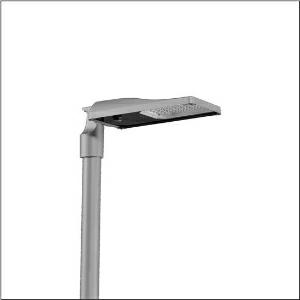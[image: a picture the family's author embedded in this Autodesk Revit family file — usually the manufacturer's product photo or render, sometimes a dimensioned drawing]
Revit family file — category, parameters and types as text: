
# Revit family: streetlight_sl_31_mini___st1_0a_5xh6d3ar08ha_e09e
name_source: partatom
category: Lighting Fixtures
units: mm (PartAtom-declared; Revit-internal decimal feet)

## family parameters
Cut with Voids When Loaded = No
Host = Face
Light Source = No
Part Type = Normal
Room Calculation Point = No
Round Connector Dimension = Use Diameter
Shared = No

## types (1)
- --- (1 x LED, 9230 lm, 68.3 W, 3000K)
    Apparent Load = 68 VA
    CIE Flux Codes = 37 72 97 100 100
    Color Rendering = 70
    Color Temperature = 3000K
    Default Elevation = 1800 mm
    Description = Streetlight SL 31 mini D4i mast luminaire for post-top, side-entry; light control with lens of PMMA; light distribution: ST1.0a, direct asymmetric distribution, for standard-compliant lighting for roads and squares; LED: luminous flux: 9.230lm, light colour: 730, colour temperature: 3000K; luminous efficacy: 135,1lm/W; control: pre-setting: logarithmic dimming characteristic, flexible luminous flux parameterisation, time-dependent luminous flux control, constant luminous flux control, power reduction, intelligent temperature release in ECG and LED module, overheat protection; luminaire housing, of diecast aluminium, Siteco® metallic grey (DB 702S), corrosivity category C5 high according to DIN EN ISO 12944; cover of toughened safety glass, transparent, opened without tools; mast flange of diecast aluminium, Siteco® metallic grey (DB 702S), spigot size: 76/60mm, mast flange included unmounted; with cable H07RN-F 2x 1.5mm², cable length: 8,5m, connection cable pre-assembled; mains connection: 220..240V, AC, 50/60Hz; power consumption (at start of service life): 68,3W / (at end of service life): 74,5W / (with reduced operation 50%): 29,5W; protection rating (complete): IP66; insulation class (complete): insulation class II (safety insulation); impact resistance: IK09; certification: CE, ENEC, ENEC+, VDE, UKCA, ZD4i; permissible operating ambient temperature for outdoor applications: -40..+50°C; packaging unit: 1 piece

Light Distribution: ST1.0a
    Height = 76 mm
    Lamp = 1 x LED
    Lamp Light Flux = 9230 lm
    Lamp Power = 68.3 W
    Lamp count = 1
    Length = 547 mm
    Luminous efficacy = 135 lm/W
    Manufacturer = Siteco
    ModVariant = No
    Model = 5XH6D3AR08HA
    Number of Poles = 1
    OnlyDefault = Yes
    Power Factor = 1
    Product Name = Streetlight SL 31 mini | ST1.0a
    Product group = mast luminaire | pylon top
    ProductGroupID = 6100
    Protection Class = Protection class II
    Protection Degree = IP 66
    RLX_Detail_Level = 1
    RLX_Emergency_Light_Flux = 0 lm
    RLX_Emergency_Type = 0
    RLX_Emergency_Type_DB = No
    RlxData = <blob elided: 24265 chars, md5=654f2af5>
    Socket = socket
    Standby Power = 0 W
    System Light Flux = 9230 lm
    System Power = 68 W
    Type Comments = factory setting: luminous flux: 100 % | dim-lin: 254 | 692 mA
    Type Image = l_1300328.jpg
    URL = http://relux.com
    VarID = @adj_019303
    Voltage = 0 V
    Weight = 0.00 kg
    Width = 265 mm

## geometry (parser evidence)
native form markers: Blend x4, Sweep x11
no freeform markers — native parametric forms only
